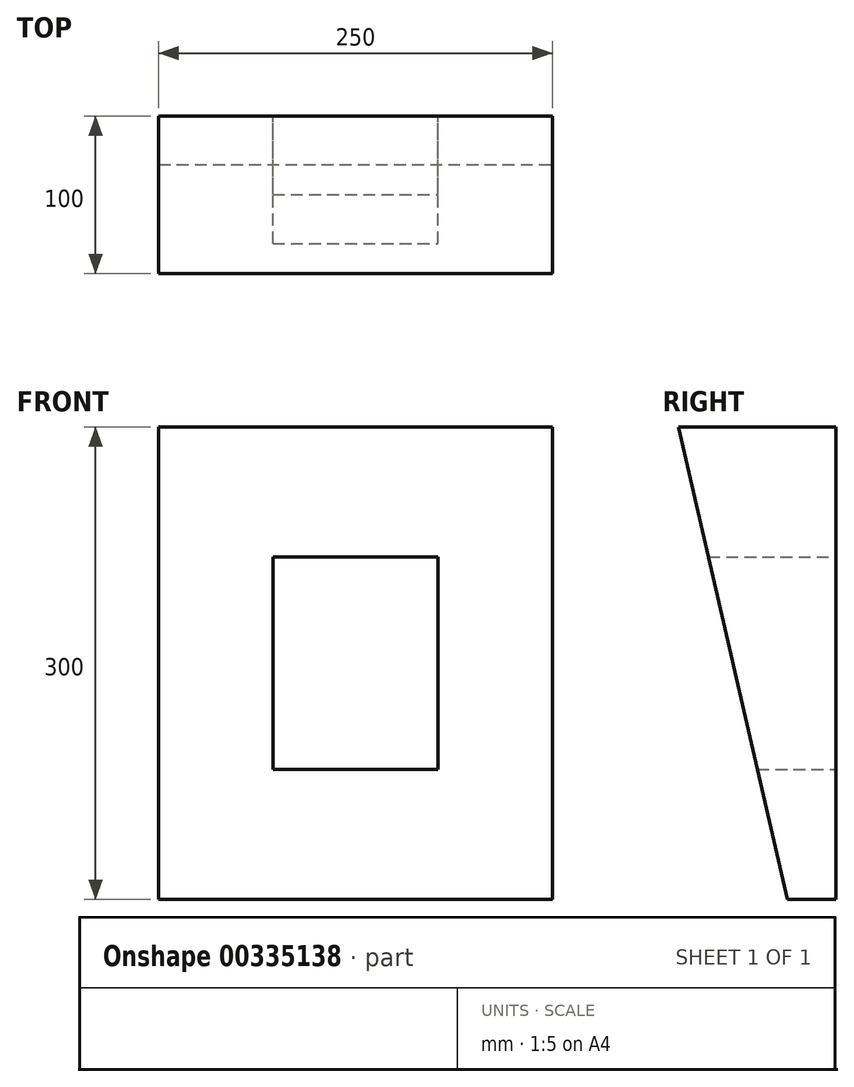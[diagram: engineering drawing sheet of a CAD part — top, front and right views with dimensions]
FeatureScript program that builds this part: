
annotation { "Feature Type Name" : "Feature", "Feature Type Description" : "" }
export const myFeature = defineFeature(function(context is Context, id is Id, definition is map)
    precondition{}
    {
        {
            var Q0;
            Q0=qCreatedBy(makeId("Front.planeOp"),FACE);
            var sketch = newSketch(context, id + "F0", { "sketchPlane" : qUnion([Q0])});
            skLineSegment(sketch, "E0.bottom", {"start": v(-62.52, 233.39) * mm, "end": v(187.48, 233.39) * mm});
            skLineSegment(sketch, "E0.top", {"start": v(-62.52, -66.61) * mm, "end": v(187.48, -66.61) * mm});
            skLineSegment(sketch, "E0.left", {"start": v(-62.52, 233.39) * mm, "end": v(-62.52, -66.61) * mm});
            skLineSegment(sketch, "E0.right", {"start": v(187.48, 233.39) * mm, "end": v(187.48, -66.61) * mm});
            skLineSegment(sketch, "E1.bottom", {"start": v(9.98, 150.89) * mm, "end": v(114.98, 150.89) * mm});
            skLineSegment(sketch, "E1.top", {"start": v(9.98, 15.89) * mm, "end": v(114.98, 15.89) * mm});
            skLineSegment(sketch, "E1.left", {"start": v(9.98, 150.89) * mm, "end": v(9.98, 15.89) * mm});
            skLineSegment(sketch, "E1.right", {"start": v(114.98, 150.89) * mm, "end": v(114.98, 15.89) * mm});
            skSolve(sketch);
        }
        {
            var Q0;
            Q0=makeQuery(id+"F0.imprint","IMPRINT",FACE,{"disambiguationData":[TD([[makeQuery(id+"F0.imprint","IMPRINT",EDGE,{"derivedFrom":sQuery(id+"F0.wireOp",EDGE,"E0.bottom")}),-1.0]])]});
            extrude(context, id + "F1", {"entities" : qUnion([Q0]), "depth" : 100 * mm, "offsetDistance" : 25 * mm});
        }
        {
            var Q0;
            Q0=makeQuery(id+"F1.opExtrude","SWEPT_FACE",FACE,{"disambiguationData":[OSD([sQuery(id+"F0.wireOp",EDGE,"E0.right")])]});
            var sketch = newSketch(context, id + "F2", { "sketchPlane" : qUnion([Q0])});
            skLineSegment(sketch, "E2", {"start": v(-100, 233.39) * mm, "end": v(-26.1, -86.88) * mm});
            skLineSegment(sketch, "E3", {"start": v(-26.1, -86.88) * mm, "end": v(-162.9, -75.3) * mm});
            skLineSegment(sketch, "E4", {"start": v(-162.9, -75.3) * mm, "end": v(-130.33, 233.39) * mm});
            skLineSegment(sketch, "E5", {"start": v(-130.33, 233.39) * mm, "end": v(-100, 233.39) * mm});
            skSolve(sketch);
        }
        {
            var Q0;
            {var subQ1=sQuery(id+"F0.wireOp",EDGE,"E0.right");var subQ2=makeQuery(id+"F1.opExtrude","CAP_EDGE",EDGE,{"disambiguationData":[OSD([subQ1])],"isStart":false});Q0=makeQuery(id+"F2.imprint","IMPRINT",FACE,{"disambiguationData":[TD([[makeQuery(id+"F2.imprint","IMPRINT",EDGE,{"derivedFrom":subQ2}),1.0]])]});}
            extrude(context, id + "F3", {"entities" : qUnion([Q0]), "operationType" : NewBodyOperationType.REMOVE, "oppositeDirection" : true, "depth" : 297 * mm, "offsetDistance" : 25 * mm});
        }
    });
